# Revit family: &SASSO 60 base ceiling round adjustable 2 lamps LS
name_source: partatom
category: Lighting Fixtures
units: mm (PartAtom-declared; Revit-internal decimal feet)

## family parameters
Cut with Voids When Loaded = Yes
Host = Face
Light Source = Yes
Part Type = Normal
Room Calculation Point = Yes
Round Connector Dimension = Use Diameter
Shared = No

## types (36) — shared parameters
Apparent Load = 12 VA
Color Filter = 16777215
Default Elevation = 1219 mm
Dimming Lamp Color Temperature Shift = <None>
Emit Shape Visible in Rendering = No
Emit from Circle Diameter = 55 mm  [stored 0.180446 ft]
Lamp = LED
Power = 0 W
Tilt Angle = -90.00°

## per-type parameters (varying)
| type | Photometric Web File |
| 2700 K 1550 lm XAL-FLOOD_11_6A15.ies | XAL-FLOOD_11_6A15.ies |
| 2700 K 1490 lm XAL-MEDIUM_A1_6433.ies | XAL-MEDIUM_A1_6433.ies |
| 2700 K 719 lm XAL-SPOT_FD_5638.ies | XAL-SPOT_FD_5638.ies |
| 3000 K 1640 lm XAL-FLOOD_11_6A15.ies | XAL-FLOOD_11_6A15.ies |
| 3000 K 1570 lm XAL-MEDIUM_A1_6433.ies | XAL-MEDIUM_A1_6433.ies |
| 3000 K 762 lm XAL-SPOT_FD_5638.ies | XAL-SPOT_FD_5638.ies |
| 4000 K 1740 lm XAL-FLOOD_11_6A15.ies | XAL-FLOOD_11_6A15.ies |
| 4000 K 1670 lm XAL-MEDIUM_A1_6433.ies | XAL-MEDIUM_A1_6433.ies |
| 4000 K 805 lm XAL-SPOT_FD_5638.ies | XAL-SPOT_FD_5638.ies |
| 2700 K 1600 lm XAL-FLOOD_7A_8935.ies | XAL-FLOOD_7A_8935.ies |
| 2700 K 1550 lm XAL-MEDIUM_6A_F6AA.ies | XAL-MEDIUM_6A_F6AA.ies |
| 2700 K 816 lm XAL-SPOT_DD_83A1.ies | XAL-SPOT_DD_83A1.ies |
| 3000 K 1690 lm XAL-FLOOD_7A_8935.ies | XAL-FLOOD_7A_8935.ies |
| 3000 K 1640 lm XAL-MEDIUM_6A_F6AA.ies | XAL-MEDIUM_6A_F6AA.ies |
| 3000 K 865 lm XAL-SPOT_DD_83A1.ies | XAL-SPOT_DD_83A1.ies |
| 4000 K 1790 lm XAL-FLOOD_7A_8935.ies | XAL-FLOOD_7A_8935.ies |
| 4000 K 1740 lm XAL-MEDIUM_6A_F6AA.ies | XAL-MEDIUM_6A_F6AA.ies |
| 4000 K 915 lm XAL-SPOT_DD_83A1.ies | XAL-SPOT_DD_83A1.ies |
| 2700 K 1720 lm XAL-FLOOD_19_7854.ies | XAL-FLOOD_19_7854.ies |
| 2700 K 1680 lm XAL-MEDIUM_9A_CBF3.ies | XAL-MEDIUM_9A_CBF3.ies |
| 2700 K 950 lm XAL-SPOT_FA_8BD0.ies | XAL-SPOT_FA_8BD0.ies |
| 3000 K 1820 lm XAL-FLOOD_19_7854.ies | XAL-FLOOD_19_7854.ies |
| 3000 K 1770 lm XAL-MEDIUM_9A_CBF3.ies | XAL-MEDIUM_9A_CBF3.ies |
| 3000 K 1010 lm XAL-SPOT_FA_8BD0.ies | XAL-SPOT_FA_8BD0.ies |
| 4000 K 1930 lm XAL-FLOOD_19_7854.ies | XAL-FLOOD_19_7854.ies |
| 4000 K 1880 lm XAL-MEDIUM_9A_CBF3.ies | XAL-MEDIUM_9A_CBF3.ies |
| 4000 K 1060 lm XAL-SPOT_FA_8BD0.ies | XAL-SPOT_FA_8BD0.ies |
| 2700 K 1750 lm XAL-FLOOD_B1_68FF.ies | XAL-FLOOD_B1_68FF.ies |
| 2700 K 1710 lm XAL-MEDIUM_37_FD73.ies | XAL-MEDIUM_37_FD73.ies |
| 2700 K 993 lm XAL-SPOT_21_A445.ies | XAL-SPOT_21_A445.ies |
| 3000 K 1840 lm XAL-FLOOD_B1_68FF.ies | XAL-FLOOD_B1_68FF.ies |
| 3000 K 1800 lm XAL-MEDIUM_37_FD73.ies | XAL-MEDIUM_37_FD73.ies |
| 3000 K 1050 lm XAL-SPOT_21_A445.ies | XAL-SPOT_21_A445.ies |
| 4000 K 1950 lm XAL-FLOOD_B1_68FF.ies | XAL-FLOOD_B1_68FF.ies |
| 4000 K 1910 lm XAL-MEDIUM_37_FD73.ies | XAL-MEDIUM_37_FD73.ies |
| 4000 K 1110 lm XAL-SPOT_21_A445.ies | XAL-SPOT_21_A445.ies |

note: [stored X ft] marks values corroborated as IEEE doubles in the binary element streams (Revit-internal decimal feet)

## geometry (parser evidence)
native form markers: Sweep x2
no freeform markers — native parametric forms only
